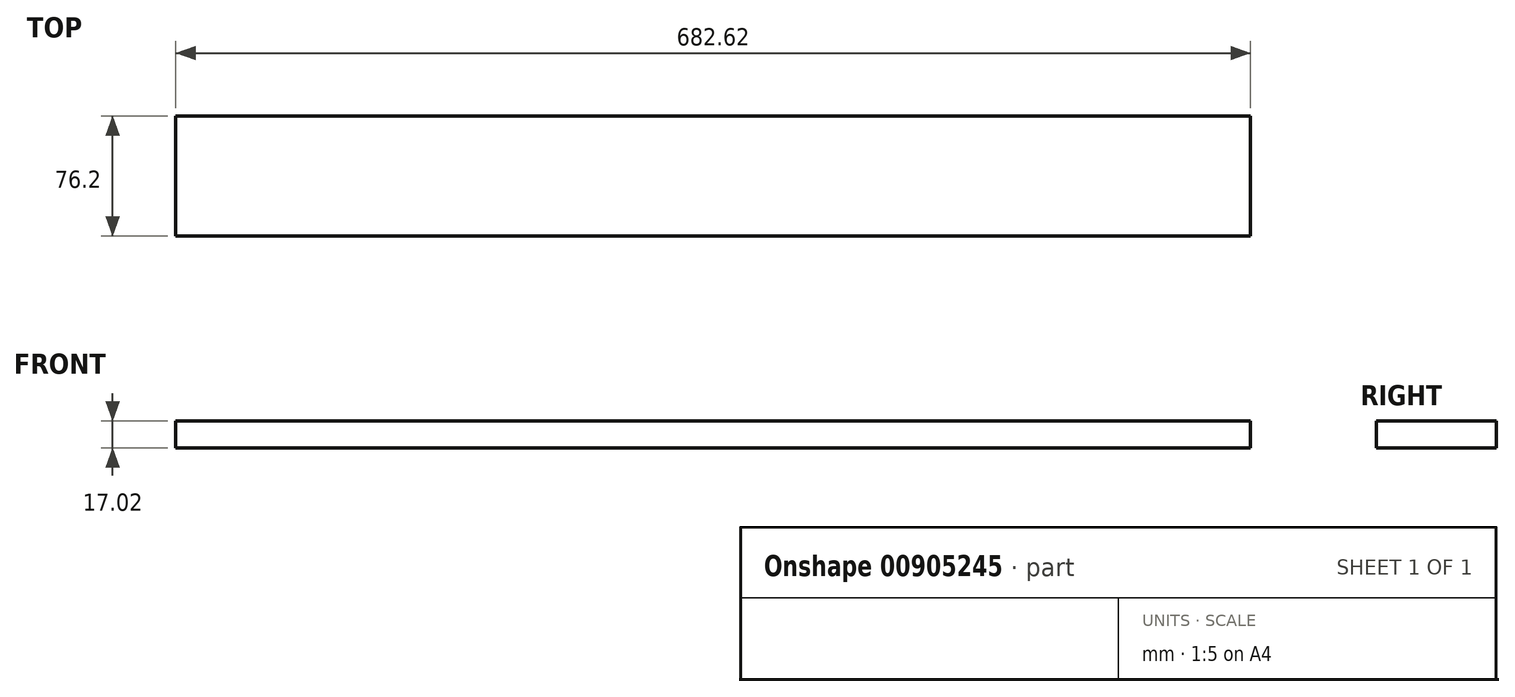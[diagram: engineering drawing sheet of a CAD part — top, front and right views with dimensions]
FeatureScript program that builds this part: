
annotation { "Feature Type Name" : "Feature", "Feature Type Description" : "" }
export const myFeature = defineFeature(function(context is Context, id is Id, definition is map)
    precondition{}
    {
        {
            var Q0;
            Q0=qCreatedBy(makeId("Top.planeOp"),FACE);
            var sketch = newSketch(context, id + "F0", { "sketchPlane" : qUnion([Q0])});
            skLineSegment(sketch, "E0.bottom", {"start": v(341.31, -38.1) * mm, "end": v(-341.31, -38.1) * mm});
            skLineSegment(sketch, "E0.top", {"start": v(341.31, 38.1) * mm, "end": v(-341.31, 38.1) * mm});
            skLineSegment(sketch, "E0.left", {"start": v(341.31, -38.1) * mm, "end": v(341.31, 38.1) * mm});
            skLineSegment(sketch, "E0.right", {"start": v(-341.31, -38.1) * mm, "end": v(-341.31, 38.1) * mm});
            skPoint(sketch, "E0.middle", {"position": v(0, 0) * mm});
            skSolve(sketch);
        }
        {
            var Q0;
            Q0=qSketchRegion(id+"F0",true);
            extrude(context, id + "F1", {"entities" : qUnion([Q0]), "oppositeDirection" : true, "offsetDistance" : 25.4 * mm, "depth" : 17.02 * mm});
        }
    });
